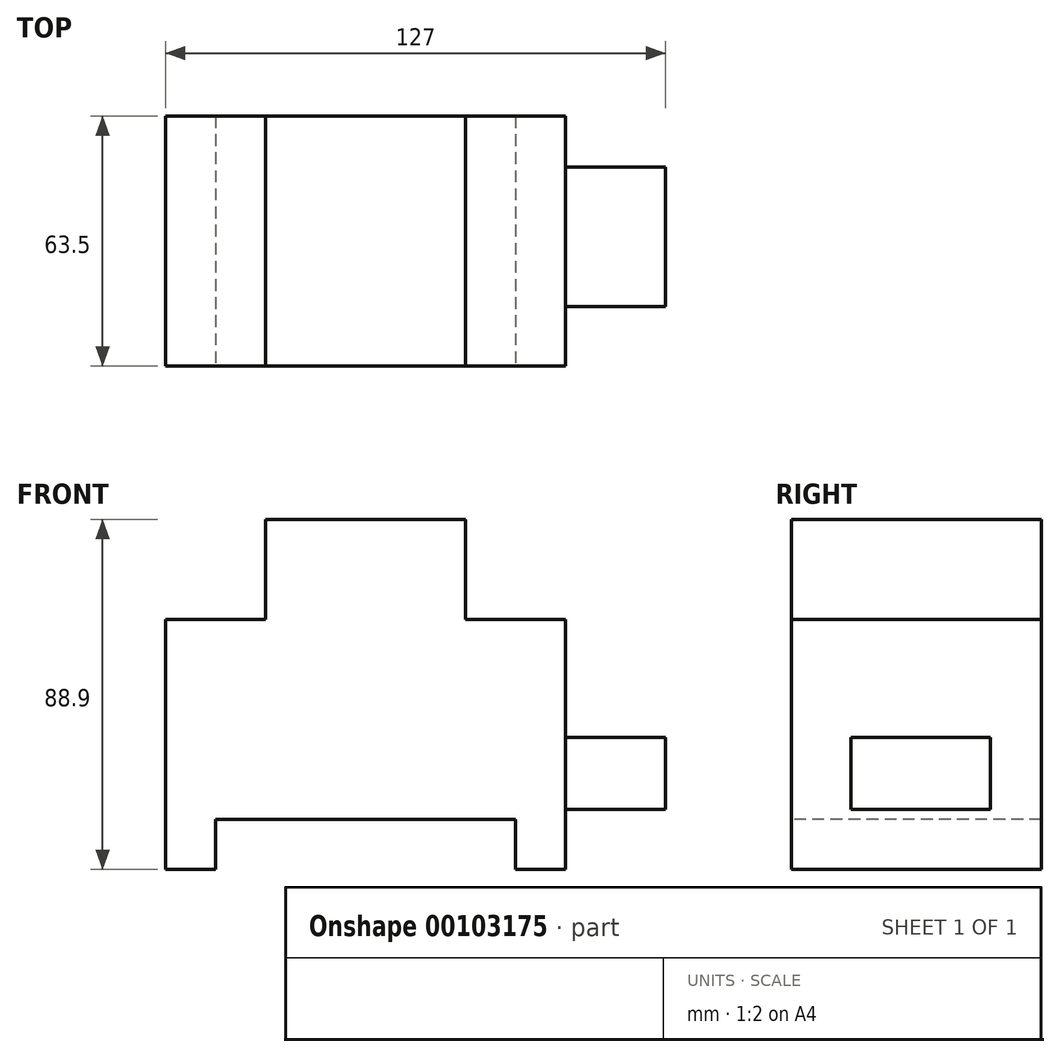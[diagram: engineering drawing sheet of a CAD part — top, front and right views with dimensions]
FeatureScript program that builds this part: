
annotation { "Feature Type Name" : "Feature", "Feature Type Description" : "" }
export const myFeature = defineFeature(function(context is Context, id is Id, definition is map)
    precondition{}
    {
        {
            var Q0;
            Q0=qCreatedBy(makeId("Front.planeOp"),FACE);
            var sketch = newSketch(context, id + "F0", { "sketchPlane" : qUnion([Q0])});
            skLineSegment(sketch, "E0.bottom", {"start": v(-74.73, 97.05) * mm, "end": v(26.87, 97.05) * mm});
            skLineSegment(sketch, "E0.top", {"start": v(-74.73, 8.15) * mm, "end": v(26.87, 8.15) * mm});
            skLineSegment(sketch, "E0.left", {"start": v(-74.73, 97.05) * mm, "end": v(-74.73, 8.15) * mm});
            skLineSegment(sketch, "E0.right", {"start": v(26.87, 97.05) * mm, "end": v(26.87, 8.15) * mm});
            skSolve(sketch);
        }
        {
            var Q0;
            Q0=makeQuery(id+"F0.imprint","IMPRINT",FACE,{"disambiguationData":[TD([[makeQuery(id+"F0.imprint","IMPRINT",EDGE,{"derivedFrom":sQuery(id+"F0.wireOp",EDGE,"E0.bottom")}),-1.0]])]});
            extrude(context, id + "F1", {"entities" : qUnion([Q0]), "depth" : 63.5 * mm});
        }
        {
            var Q0;
            Q0=makeQuery(id+"F1.opExtrude","CAP_FACE",FACE,{"disambiguationData":[OSD([sQuery(id+"F0.wireOp",EDGE,"E0.bottom"),sQuery(id+"F0.wireOp",EDGE,"E0.top"),sQuery(id+"F0.wireOp",EDGE,"E0.left"),sQuery(id+"F0.wireOp",EDGE,"E0.right")])],"isStart":false});
            var sketch = newSketch(context, id + "F2", { "sketchPlane" : qUnion([Q0])});
            skLineSegment(sketch, "E1.bottom", {"start": v(-74.73, 97.05) * mm, "end": v(-49.33, 97.05) * mm});
            skLineSegment(sketch, "E1.top", {"start": v(-74.73, 71.65) * mm, "end": v(-49.33, 71.65) * mm});
            skLineSegment(sketch, "E1.left", {"start": v(-74.73, 97.05) * mm, "end": v(-74.73, 71.65) * mm});
            skLineSegment(sketch, "E1.right", {"start": v(-49.33, 97.05) * mm, "end": v(-49.33, 71.65) * mm});
            skSolve(sketch);
        }
        {
            var Q0;
            Q0 = qSketchRegion(id + "F2", true);
            extrude(context, id + "F3", {"entities" : qUnion([Q0]), "operationType" : NewBodyOperationType.REMOVE, "oppositeDirection" : true, "depth" : 63.5 * mm});
        }
        {
            var Q0;
            Q0=makeQuery(id+"F1.opExtrude","CAP_FACE",FACE,{"disambiguationData":[OSD([sQuery(id+"F0.wireOp",EDGE,"E0.bottom"),sQuery(id+"F0.wireOp",EDGE,"E0.top"),sQuery(id+"F0.wireOp",EDGE,"E0.left"),sQuery(id+"F0.wireOp",EDGE,"E0.right")])],"isStart":false});
            var sketch = newSketch(context, id + "F4", { "sketchPlane" : qUnion([Q0])});
            skLineSegment(sketch, "E2.bottom", {"start": v(26.87, 97.05) * mm, "end": v(1.47, 97.05) * mm});
            skLineSegment(sketch, "E2.top", {"start": v(26.87, 71.65) * mm, "end": v(1.47, 71.65) * mm});
            skLineSegment(sketch, "E2.left", {"start": v(26.87, 97.05) * mm, "end": v(26.87, 71.65) * mm});
            skLineSegment(sketch, "E2.right", {"start": v(1.47, 97.05) * mm, "end": v(1.47, 71.65) * mm});
            skSolve(sketch);
        }
        {
            var Q0;
            Q0=makeQuery(id+"F4.imprint","IMPRINT",FACE,{"disambiguationData":[TD([[makeQuery(id+"F4.imprint","IMPRINT",EDGE,{"derivedFrom":sQuery(id+"F4.wireOp",EDGE,"E2.bottom")}),-1.0]])]});
            extrude(context, id + "F5", {"entities" : qUnion([Q0]), "operationType" : NewBodyOperationType.REMOVE, "oppositeDirection" : true, "depth" : 63.5 * mm});
        }
        {
            var Q0;
            Q0=makeQuery(id+"F1.opExtrude","CAP_FACE",FACE,{"disambiguationData":[OSD([sQuery(id+"F0.wireOp",EDGE,"E0.bottom"),sQuery(id+"F0.wireOp",EDGE,"E0.top"),sQuery(id+"F0.wireOp",EDGE,"E0.left"),sQuery(id+"F0.wireOp",EDGE,"E0.right")])],"isStart":false});
            var sketch = newSketch(context, id + "F6", { "sketchPlane" : qUnion([Q0])});
            skLineSegment(sketch, "E3.bottom", {"start": v(-62.03, 8.15) * mm, "end": v(14.17, 8.15) * mm});
            skLineSegment(sketch, "E3.top", {"start": v(-62.03, 20.85) * mm, "end": v(14.17, 20.85) * mm});
            skLineSegment(sketch, "E3.left", {"start": v(-62.03, 8.15) * mm, "end": v(-62.03, 20.85) * mm});
            skLineSegment(sketch, "E3.right", {"start": v(14.17, 8.15) * mm, "end": v(14.17, 20.85) * mm});
            skSolve(sketch);
        }
        {
            var Q0;
            Q0=makeQuery(id+"F6.imprint","IMPRINT",FACE,{"disambiguationData":[TD([[makeQuery(id+"F6.imprint","IMPRINT",EDGE,{"derivedFrom":sQuery(id+"F6.wireOp",EDGE,"E3.bottom")}),1.0]])]});
            extrude(context, id + "F7", {"entities" : qUnion([Q0]), "operationType" : NewBodyOperationType.REMOVE, "oppositeDirection" : true, "depth" : 63.5 * mm});
        }
        {
            var Q0;
            Q0=makeQuery(id+"F1.opExtrude","SWEPT_FACE",FACE,{"disambiguationData":[OSD([sQuery(id+"F0.wireOp",EDGE,"E0.right")])]});
            var sketch = newSketch(context, id + "F8", { "sketchPlane" : qUnion([Q0])});
            skLineSegment(sketch, "E4.bottom", {"start": v(-48.39, 41.64) * mm, "end": v(-12.92, 41.64) * mm});
            skLineSegment(sketch, "E4.top", {"start": v(-48.39, 23.4) * mm, "end": v(-12.92, 23.4) * mm});
            skLineSegment(sketch, "E4.left", {"start": v(-48.39, 41.64) * mm, "end": v(-48.39, 23.4) * mm});
            skLineSegment(sketch, "E4.right", {"start": v(-12.92, 41.64) * mm, "end": v(-12.92, 23.4) * mm});
            skSolve(sketch);
        }
        {
            var Q0;
            Q0 = qSketchRegion(id + "F8", true);
            extrude(context, id + "F9", {"entities" : qUnion([Q0]), "operationType" : NewBodyOperationType.ADD, "depth" : 25.4 * mm});
        }
    });
